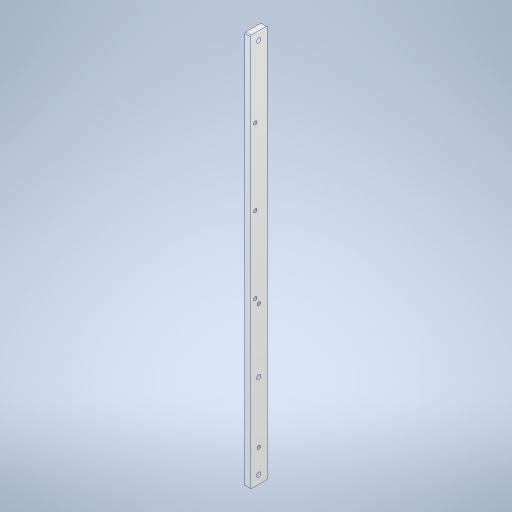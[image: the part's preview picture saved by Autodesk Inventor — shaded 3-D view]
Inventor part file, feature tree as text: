
AUTODESK INVENTOR PART (.ipt)
format: ipt  version: 2024 (Build 280153000, 153)  size: 285,696 bytes
history: native  units: mm
features: sketch x4, hole x3, projected_geometry x2, extrude x1, fillet x1
ambient origin geometry x8: Origin, YZ Plane, XZ Plane, XY Plane, X Axis, Y Axis, Z Axis, Center Point
bodies: Solid1 (feature_tree)
feature tree (11):
  extrude  "Extrusion1"  Depth=20.0mm
  hole  "Hole1"  [1 undecoded]
  hole  "Hole2"  [1 undecoded]
  fillet  "Fillet1"  Radius=72.0mm
  hole  "Hole3"  [1 undecoded]
  sketch  "Sketch1"  dims[d0=465.0mm d1=20.0mm]
  sketch  "Sketch2"  dims[d2=6.35mm d3=0.0mm d4=10.0mm]
  projected_geometry  "Projected Loop1"
  sketch  "Sketch3"  dims[d5=10.0mm d6=100.0mm]
  projected_geometry  "Projected Loop2"
  sketch  "Sketch4"  dims[d7=5.3mm d8=6.0mm d9=4.0mm d10=2.0mm d11=90.0deg d12=8.0mm d13=20.594885mm d14=72.0mm d15=4.134mm d16=10.0mm d17=4.0mm d18=2.0mm d19=90.0deg d20=8.0mm d21=20.594885mm d22=147.0mm d23=1.0mm d24=180.0mm d25=6.0mm d26=4.134mm d27=10.0mm d28=4.0mm d29=2.0mm d30=90.0deg d31=8.0mm d32=20.594885mm]
note: 3 required parameter values undecoded (feature->parameter linkage not recoverable at this tier; creation-order binding heuristic only, values carry confidence <= 0.55)
